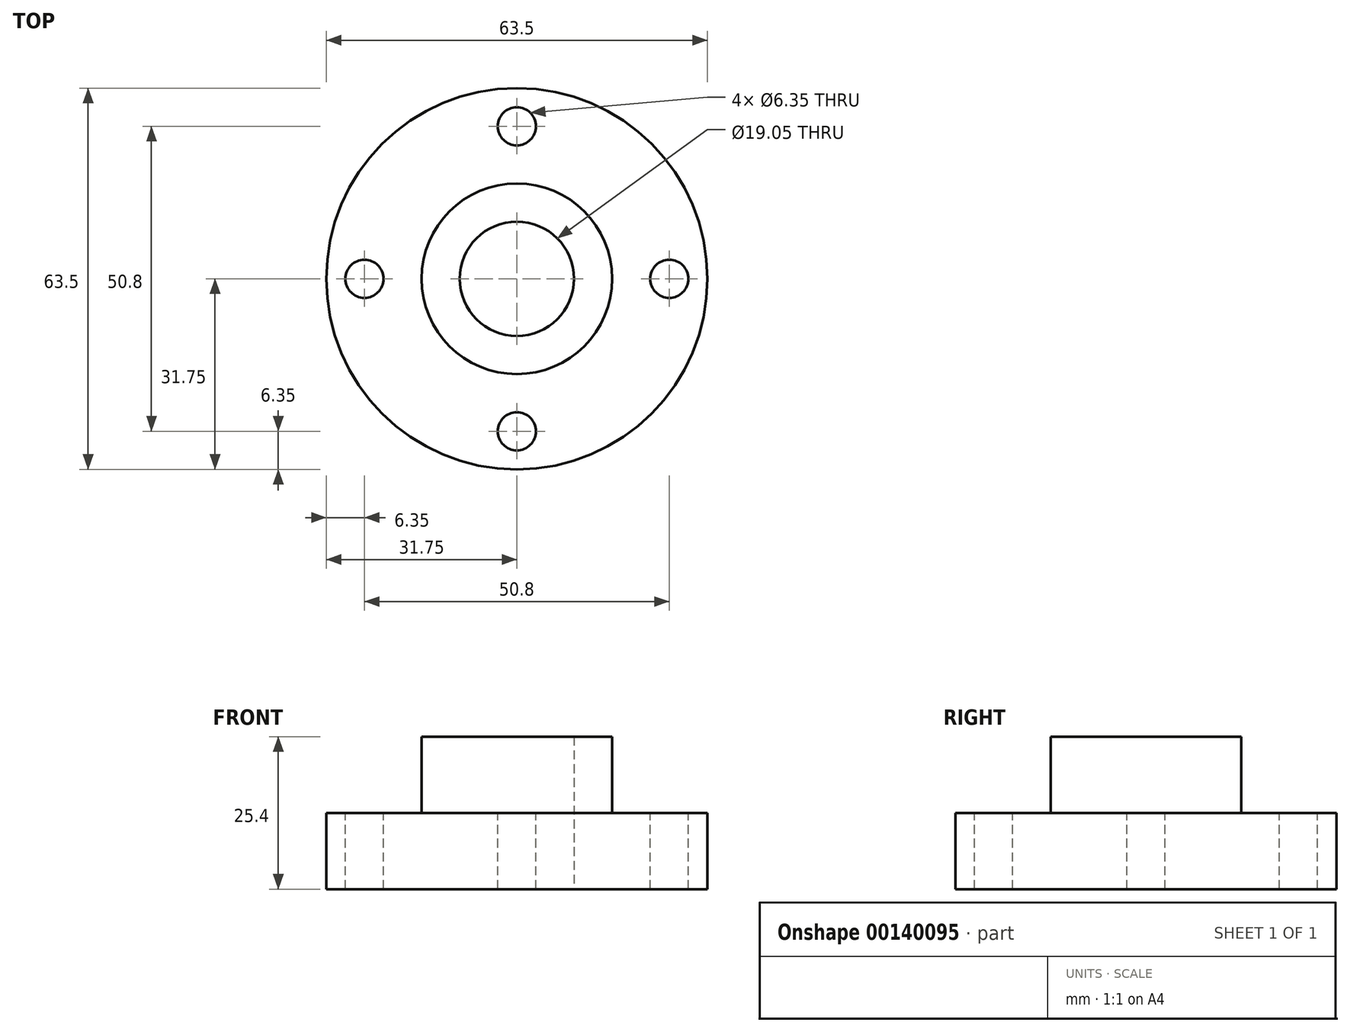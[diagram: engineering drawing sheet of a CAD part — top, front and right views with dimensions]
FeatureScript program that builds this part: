
annotation { "Feature Type Name" : "Feature", "Feature Type Description" : "" }
export const myFeature = defineFeature(function(context is Context, id is Id, definition is map)
    precondition{}
    {
        {
            var Q0;
            Q0=qCreatedBy(makeId("Top.planeOp"),FACE);
            var sketch = newSketch(context, id + "F0", { "sketchPlane" : qUnion([Q0])});
            skCircle(sketch, "E0", {"center": v(0, 0) * mm, "radius": 9.53 * mm});
            skCircle(sketch, "E1", {"center": v(0, 0) * mm, "radius": 15.88 * mm});
            skCircle(sketch, "E2", {"center": v(0, 0) * mm, "radius": 31.75 * mm});
            skCircle(sketch, "E3", {"center": v(0, 25.4) * mm, "radius": 3.18 * mm});
            skLineSegment(sketch, "E4", {"start": v(0, 30.15) * mm, "end": v(0, -32.21) * mm, "construction": true});
            skLineSegment(sketch, "E5", {"start": v(-31.23, 0) * mm, "end": v(46.4, 0) * mm, "construction": true});
            skPoint(sketch, "E6.center", {"position": v(0, 7.72) * mm});
            skLineSegment(sketch, "E6.anchor1", {"start": v(0, 7.72) * mm, "end": v(0, 25.4) * mm, "construction": true});
            skCircle(sketch, "E7.1.0", {"center": v(25.4, 0) * mm, "radius": 3.18 * mm});
            skCircle(sketch, "E7.2.0", {"center": v(0, -25.4) * mm, "radius": 3.18 * mm});
            skCircle(sketch, "E7.3.0", {"center": v(-25.4, 0) * mm, "radius": 3.18 * mm});
            skLineSegment(sketch, "E7.anchor1", {"start": v(0, 0) * mm, "end": v(0, 25.4) * mm, "construction": true});
            skLineSegment(sketch, "E7.anchor2", {"start": v(0, 0) * mm, "end": v(-25.4, 0) * mm, "construction": true});
            skSolve(sketch);
        }
        {
            var Q0;
            Q0=makeQuery(id+"F0.imprint","IMPRINT",FACE,{"disambiguationData":[TD([[makeQuery(id+"F0.imprint","IMPRINT",EDGE,{"derivedFrom":sQuery(id+"F0.wireOp",EDGE,"E1")}),-1.0]])]});
            extrude(context, id + "F1", {"entities" : qUnion([Q0]), "oppositeDirection" : true, "depth" : 12.7 * mm});
        }
        {
            var Q0;
            Q0=makeQuery(id+"F0.imprint","IMPRINT",FACE,{"disambiguationData":[TD([[makeQuery(id+"F0.imprint","IMPRINT",EDGE,{"derivedFrom":sQuery(id+"F0.wireOp",EDGE,"E0")}),-1.0]])]});
            extrude(context, id + "F2", {"entities" : qUnion([Q0]), "operationType" : NewBodyOperationType.ADD, "endBound" : BoundingType.SYMMETRIC, "depth" : 25.4 * mm});
        }
    });
